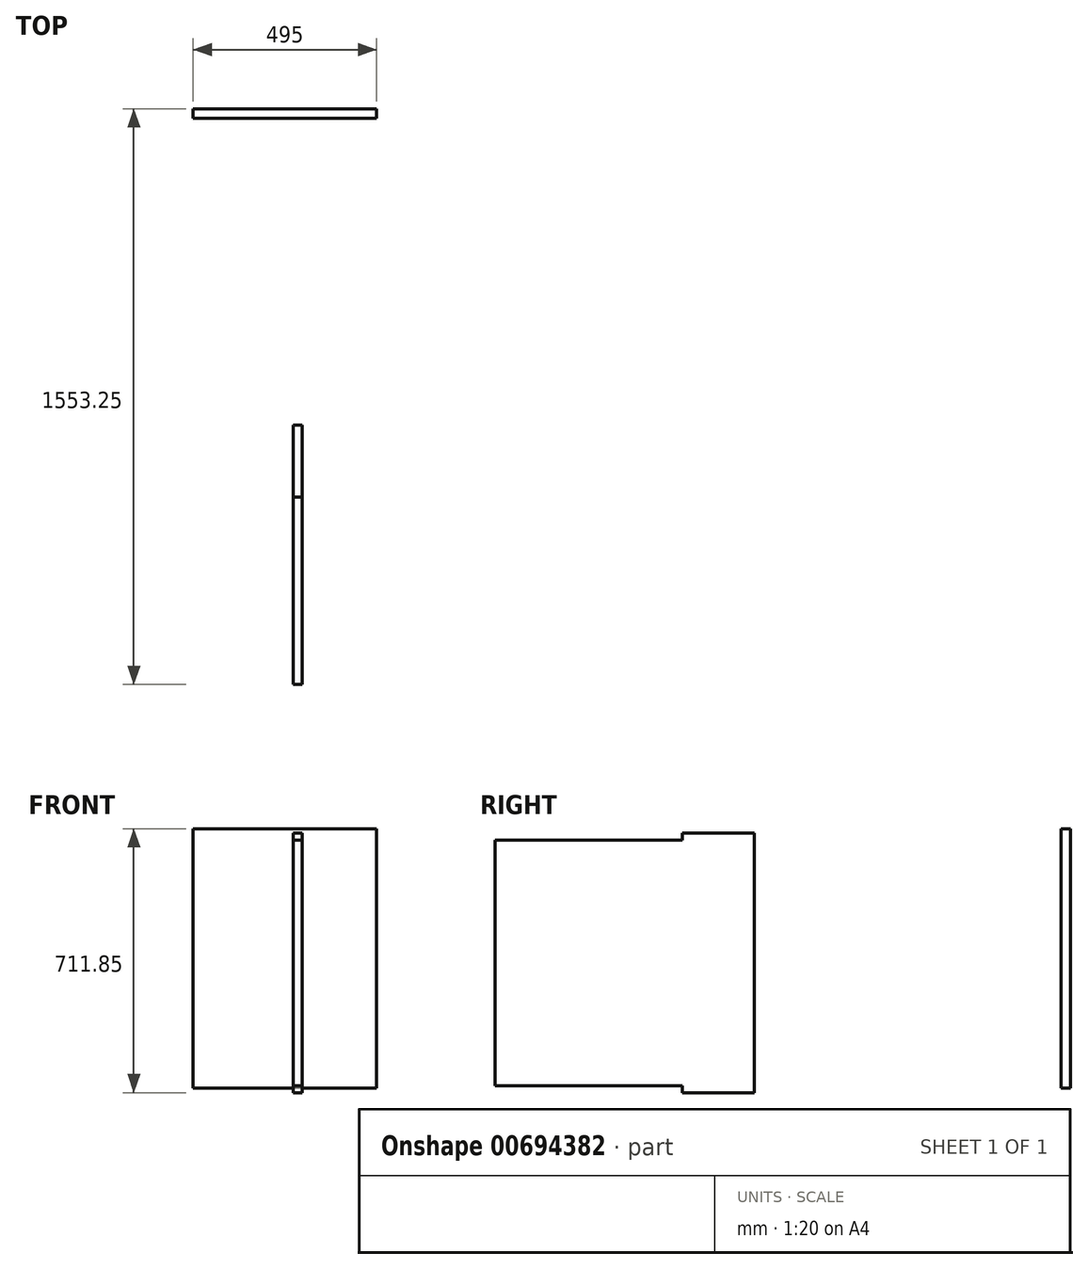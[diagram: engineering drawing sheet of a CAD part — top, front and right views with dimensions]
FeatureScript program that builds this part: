
annotation { "Feature Type Name" : "Feature", "Feature Type Description" : "" }
export const myFeature = defineFeature(function(context is Context, id is Id, definition is map)
    precondition{}
    {
        {
            var Q0;
            Q0=qCreatedBy(makeId("Front.planeOp"),FACE);
            var sketch = newSketch(context, id + "F0", { "sketchPlane" : qUnion([Q0])});
            skLineSegment(sketch, "E0.bottom", {"start": v(225.33, 348.6) * mm, "end": v(-269.67, 348.6) * mm});
            skLineSegment(sketch, "E0.top", {"start": v(225.33, -351.4) * mm, "end": v(-269.67, -351.4) * mm});
            skLineSegment(sketch, "E0.left", {"start": v(225.33, 348.6) * mm, "end": v(225.33, -351.4) * mm});
            skLineSegment(sketch, "E0.right", {"start": v(-269.67, 348.6) * mm, "end": v(-269.67, -351.4) * mm});
            skSolve(sketch);
        }
        {
            var Q0;
            Q0 = qSketchRegion(id + "F0", true);
            extrude(context, id + "F1", {"entities" : qUnion([Q0]), "depth" : 25 * mm, "offsetDistance" : 25 * mm});
        }
        {
            var Q0;
            Q0=qCreatedBy(makeId("Right.planeOp"),FACE);
            var sketch = newSketch(context, id + "F2", { "sketchPlane" : qUnion([Q0])});
            skLineSegment(sketch, "E1", {"start": v(-853.25, 336.74) * mm, "end": v(-853.25, -363.26) * mm});
            skLineSegment(sketch, "E2", {"start": v(-853.25, -363.26) * mm, "end": v(-1048.25, -363.26) * mm});
            skLineSegment(sketch, "E3", {"start": v(-1048.25, -363.26) * mm, "end": v(-1048.25, -344.26) * mm});
            skLineSegment(sketch, "E4", {"start": v(-1048.25, -344.26) * mm, "end": v(-1553.25, -344.26) * mm});
            skLineSegment(sketch, "E5", {"start": v(-1553.25, -344.26) * mm, "end": v(-1553.25, 317.74) * mm});
            skLineSegment(sketch, "E6", {"start": v(-1553.25, 317.74) * mm, "end": v(-1048.25, 317.74) * mm});
            skLineSegment(sketch, "E7", {"start": v(-1048.25, 317.74) * mm, "end": v(-1048.25, 336.74) * mm});
            skLineSegment(sketch, "E8", {"start": v(-1048.25, 336.74) * mm, "end": v(-853.25, 336.74) * mm});
            skSolve(sketch);
        }
        {
            var Q0;
            Q0 = qSketchRegion(id + "F2", true);
            extrude(context, id + "F3", {"entities" : qUnion([Q0]), "depth" : 25 * mm, "offsetDistance" : 25 * mm});
        }
    });
